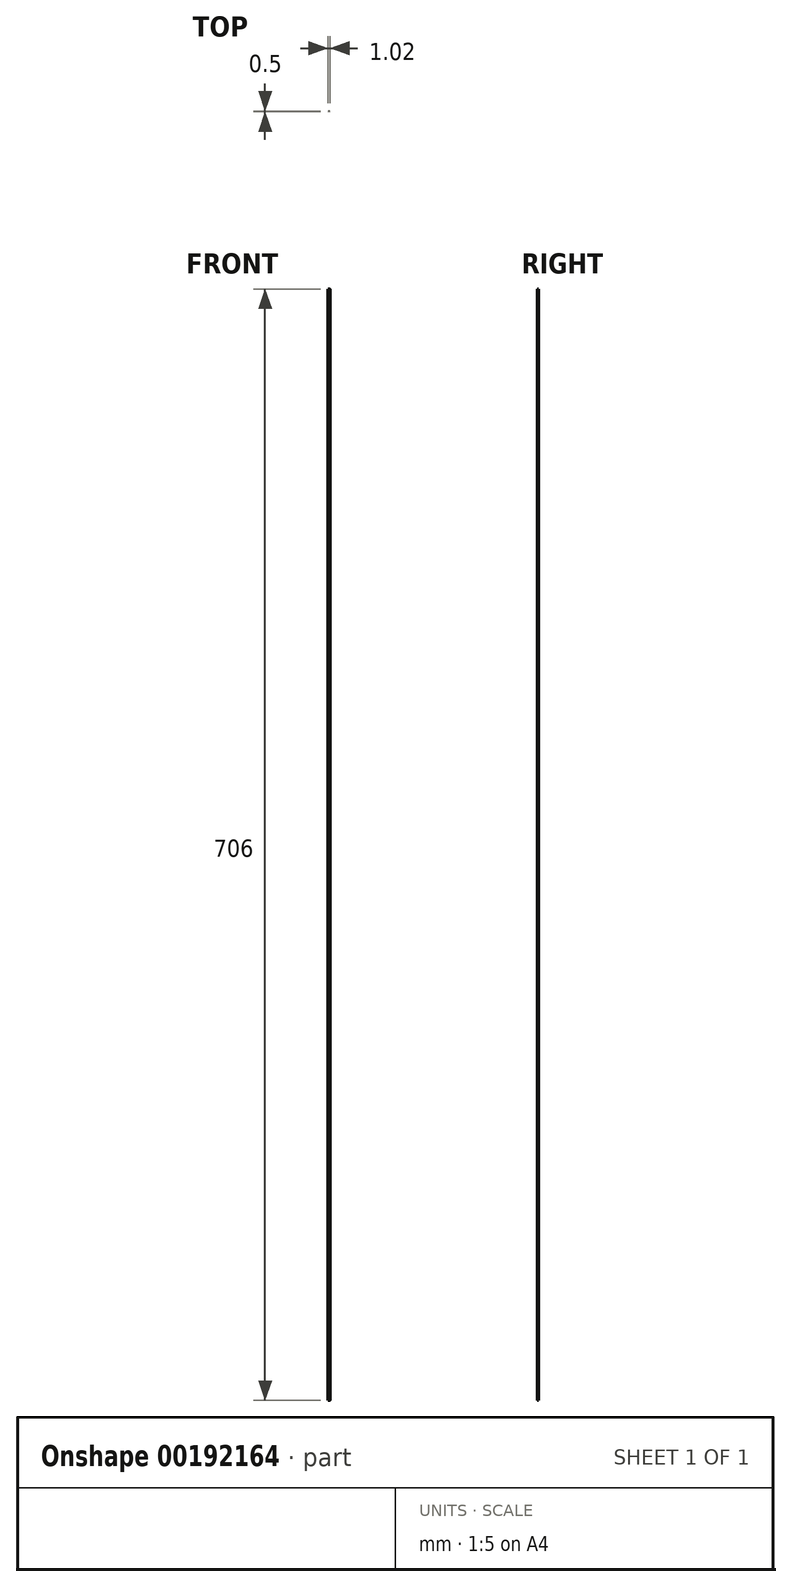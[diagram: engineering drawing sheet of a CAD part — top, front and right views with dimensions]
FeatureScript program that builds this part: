
annotation { "Feature Type Name" : "Feature", "Feature Type Description" : "" }
export const myFeature = defineFeature(function(context is Context, id is Id, definition is map)
    precondition{}
    {
        {
            var Q0;
            Q0=qCreatedBy(makeId("Top.planeOp"),FACE);
            var sketch = newSketch(context, id + "F0", { "sketchPlane" : qUnion([Q0])});
            skLineSegment(sketch, "E0.0", {"start": v(58.77, 41.7) * mm, "end": v(62.07, 38.4) * mm});
            skPoint(sketch, "E1.0", {"position": v(57.66, 41.92) * mm});
            skArc(sketch, "E2.0", {"start": v(57.02, 40.97) * mm, "mid": v(57.66, 41.92) * mm, "end": v(58.77, 41.7) * mm});
            skLineSegment(sketch, "E3.0", {"start": v(57.02, 38.85) * mm, "end": v(57.02, 40.97) * mm});
            skArc(sketch, "E4.0", {"start": v(55.97, 37.8) * mm, "mid": v(56.71, 38.11) * mm, "end": v(57.02, 38.85) * mm});
            skArc(sketch, "E5.0.0", {"start": v(63.56, 29.14) * mm, "mid": v(64.59, 29.83) * mm, "end": v(65.8, 30.07) * mm});
            skLineSegment(sketch, "E5.0.1", {"start": v(65.8, 30.07) * mm, "end": v(69.22, 30.07) * mm});
            skArc(sketch, "E5.0.2", {"start": v(69.22, 30.07) * mm, "mid": v(70.43, 29.83) * mm, "end": v(71.46, 29.14) * mm});
            skLineSegment(sketch, "E5.0.3", {"start": v(71.46, 29.14) * mm, "end": v(74.7, 25.92) * mm});
            skArc(sketch, "E5.0.4", {"start": v(74.7, 25.92) * mm, "mid": v(74.93, 24.74) * mm, "end": v(73.93, 24.08) * mm});
            skLineSegment(sketch, "E5.0.5", {"start": v(73.93, 24.08) * mm, "end": v(71.8, 24.08) * mm});
            skArc(sketch, "E5.0.6", {"start": v(71.8, 24.08) * mm, "mid": v(71.06, 23.77) * mm, "end": v(70.75, 23.03) * mm});
            skLineSegment(sketch, "E5.0.7", {"start": v(70.75, 23.03) * mm, "end": v(70.75, 22.92) * mm});
            skArc(sketch, "E5.0.8", {"start": v(70.75, 22.92) * mm, "mid": v(71.06, 22.17) * mm, "end": v(71.8, 21.87) * mm});
            skLineSegment(sketch, "E5.0.9", {"start": v(71.8, 21.87) * mm, "end": v(72.83, 21.87) * mm});
            skArc(sketch, "E5.0.10", {"start": v(72.83, 21.87) * mm, "mid": v(73.34, 22.37) * mm, "end": v(73.84, 21.87) * mm});
            skLineSegment(sketch, "E5.0.11", {"start": v(73.84, 21.87) * mm, "end": v(77.06, 21.87) * mm});
            skArc(sketch, "E5.0.12", {"start": v(77.06, 21.87) * mm, "mid": v(77.57, 22.37) * mm, "end": v(78.08, 21.87) * mm});
            skArc(sketch, "E5.0.13", {"start": v(78.08, 21.87) * mm, "mid": v(79.6, 22.48) * mm, "end": v(80.21, 24) * mm});
            skArc(sketch, "E5.0.14", {"start": v(80.21, 24) * mm, "mid": v(79.7, 24.5) * mm, "end": v(80.21, 25.02) * mm});
            skLineSegment(sketch, "E5.0.15", {"start": v(80.21, 25.02) * mm, "end": v(80.21, 28.23) * mm});
            skArc(sketch, "E5.0.16", {"start": v(80.21, 28.23) * mm, "mid": v(79.7, 28.74) * mm, "end": v(80.21, 29.25) * mm});
            skLineSegment(sketch, "E5.0.17", {"start": v(80.21, 29.25) * mm, "end": v(80.21, 30.28) * mm});
            skArc(sketch, "E5.0.18", {"start": v(80.21, 30.28) * mm, "mid": v(79.9, 31.02) * mm, "end": v(79.16, 31.33) * mm});
            skLineSegment(sketch, "E5.0.19", {"start": v(79.16, 31.33) * mm, "end": v(79.05, 31.33) * mm});
            skArc(sketch, "E5.0.20", {"start": v(79.05, 31.33) * mm, "mid": v(78.3, 31.02) * mm, "end": v(78, 30.28) * mm});
            skLineSegment(sketch, "E5.0.21", {"start": v(78, 30.28) * mm, "end": v(78, 28.16) * mm});
            skArc(sketch, "E5.0.22", {"start": v(78, 28.16) * mm, "mid": v(77.37, 27.21) * mm, "end": v(76.25, 27.44) * mm});
            skLineSegment(sketch, "E5.0.23", {"start": v(76.25, 27.44) * mm, "end": v(72.95, 30.73) * mm});
            skArc(sketch, "E5.0.24", {"start": v(72.95, 30.73) * mm, "mid": v(72.26, 31.76) * mm, "end": v(72.02, 32.97) * mm});
            skLineSegment(sketch, "E5.0.25", {"start": v(72.02, 32.97) * mm, "end": v(72.02, 36.16) * mm});
            skArc(sketch, "E5.0.26", {"start": v(72.02, 36.16) * mm, "mid": v(72.26, 37.38) * mm, "end": v(72.95, 38.4) * mm});
            skLineSegment(sketch, "E5.0.27", {"start": v(72.95, 38.4) * mm, "end": v(76.25, 41.7) * mm});
            skArc(sketch, "E5.0.28", {"start": v(76.25, 41.7) * mm, "mid": v(77.37, 41.92) * mm, "end": v(78, 40.97) * mm});
            skLineSegment(sketch, "E5.0.29", {"start": v(78, 40.97) * mm, "end": v(78, 38.85) * mm});
            skArc(sketch, "E5.0.30", {"start": v(78, 38.85) * mm, "mid": v(78.3, 38.11) * mm, "end": v(79.05, 37.8) * mm});
            skLineSegment(sketch, "E5.0.31", {"start": v(79.05, 37.8) * mm, "end": v(79.16, 37.8) * mm});
            skArc(sketch, "E5.0.32", {"start": v(79.16, 37.8) * mm, "mid": v(79.9, 38.11) * mm, "end": v(80.21, 38.85) * mm});
            skLineSegment(sketch, "E5.0.33", {"start": v(80.21, 38.85) * mm, "end": v(80.21, 39.88) * mm});
            skArc(sketch, "E5.0.34", {"start": v(80.21, 39.88) * mm, "mid": v(79.7, 40.4) * mm, "end": v(80.21, 40.9) * mm});
            skLineSegment(sketch, "E5.0.35", {"start": v(80.21, 40.9) * mm, "end": v(80.21, 44.12) * mm});
            skArc(sketch, "E5.0.36", {"start": v(80.21, 44.12) * mm, "mid": v(79.7, 44.62) * mm, "end": v(80.21, 45.13) * mm});
            skArc(sketch, "E5.0.37", {"start": v(80.21, 45.13) * mm, "mid": v(79.6, 46.65) * mm, "end": v(78.08, 47.27) * mm});
            skArc(sketch, "E5.0.38", {"start": v(78.08, 47.27) * mm, "mid": v(77.57, 46.76) * mm, "end": v(77.06, 47.27) * mm});
            skLineSegment(sketch, "E5.0.39", {"start": v(77.06, 47.27) * mm, "end": v(73.84, 47.27) * mm});
            skArc(sketch, "E5.0.40", {"start": v(73.84, 47.27) * mm, "mid": v(73.34, 46.76) * mm, "end": v(72.83, 47.27) * mm});
            skLineSegment(sketch, "E5.0.41", {"start": v(72.83, 47.27) * mm, "end": v(71.8, 47.27) * mm});
            skArc(sketch, "E5.0.42", {"start": v(71.8, 47.27) * mm, "mid": v(71.06, 46.96) * mm, "end": v(70.75, 46.22) * mm});
            skLineSegment(sketch, "E5.0.43", {"start": v(70.75, 46.22) * mm, "end": v(70.75, 46.1) * mm});
            skArc(sketch, "E5.0.44", {"start": v(70.75, 46.1) * mm, "mid": v(71.06, 45.36) * mm, "end": v(71.8, 45.06) * mm});
            skLineSegment(sketch, "E5.0.45", {"start": v(71.8, 45.06) * mm, "end": v(73.99, 45.06) * mm});
            skArc(sketch, "E5.0.46", {"start": v(73.99, 45.06) * mm, "mid": v(74.94, 44.42) * mm, "end": v(74.72, 43.3) * mm});
            skLineSegment(sketch, "E5.0.47", {"start": v(74.72, 43.3) * mm, "end": v(71.4, 39.99) * mm});
            skArc(sketch, "E5.0.48", {"start": v(71.4, 39.99) * mm, "mid": v(70.38, 39.3) * mm, "end": v(69.17, 39.06) * mm});
            skLineSegment(sketch, "E5.0.49", {"start": v(69.17, 39.06) * mm, "end": v(65.86, 39.06) * mm});
            skArc(sketch, "E5.0.50", {"start": v(65.86, 39.06) * mm, "mid": v(64.64, 39.3) * mm, "end": v(63.61, 39.99) * mm});
            skLineSegment(sketch, "E5.0.51", {"start": v(63.61, 39.99) * mm, "end": v(60.3, 43.3) * mm});
            skArc(sketch, "E5.0.52", {"start": v(60.3, 43.3) * mm, "mid": v(60.08, 44.42) * mm, "end": v(61.03, 45.06) * mm});
            skLineSegment(sketch, "E5.0.53", {"start": v(61.03, 45.06) * mm, "end": v(63.22, 45.06) * mm});
            skArc(sketch, "E5.0.54", {"start": v(63.22, 45.06) * mm, "mid": v(63.97, 45.36) * mm, "end": v(64.27, 46.1) * mm});
            skLineSegment(sketch, "E5.0.55", {"start": v(64.27, 46.1) * mm, "end": v(64.27, 46.22) * mm});
            skArc(sketch, "E5.0.56", {"start": v(64.27, 46.22) * mm, "mid": v(63.97, 46.96) * mm, "end": v(63.22, 47.27) * mm});
            skLineSegment(sketch, "E5.0.57", {"start": v(63.22, 47.27) * mm, "end": v(62.2, 47.27) * mm});
            skArc(sketch, "E5.0.58", {"start": v(62.2, 47.27) * mm, "mid": v(61.69, 46.76) * mm, "end": v(61.18, 47.27) * mm});
            skLineSegment(sketch, "E5.0.59", {"start": v(61.18, 47.27) * mm, "end": v(57.96, 47.27) * mm});
            skArc(sketch, "E5.0.60", {"start": v(57.96, 47.27) * mm, "mid": v(57.45, 46.76) * mm, "end": v(56.95, 47.27) * mm});
            skArc(sketch, "E5.0.61", {"start": v(56.95, 47.27) * mm, "mid": v(55.43, 46.65) * mm, "end": v(54.81, 45.13) * mm});
            skArc(sketch, "E5.0.62", {"start": v(54.81, 45.13) * mm, "mid": v(55.32, 44.62) * mm, "end": v(54.81, 44.12) * mm});
            skLineSegment(sketch, "E5.0.63", {"start": v(54.81, 44.12) * mm, "end": v(54.81, 40.9) * mm});
            skArc(sketch, "E5.0.64", {"start": v(54.81, 40.9) * mm, "mid": v(55.32, 40.4) * mm, "end": v(54.81, 39.88) * mm});
            skLineSegment(sketch, "E5.0.65", {"start": v(54.81, 39.88) * mm, "end": v(54.81, 38.85) * mm});
            skArc(sketch, "E5.0.66", {"start": v(54.81, 38.85) * mm, "mid": v(55.12, 38.11) * mm, "end": v(55.86, 37.8) * mm});
            skLineSegment(sketch, "E5.0.67", {"start": v(55.86, 37.8) * mm, "end": v(55.97, 37.8) * mm});
            skArc(sketch, "E5.0.72", {"start": v(62.07, 38.4) * mm, "mid": v(62.76, 37.38) * mm, "end": v(63, 36.16) * mm});
            skLineSegment(sketch, "E5.0.73", {"start": v(63, 36.16) * mm, "end": v(63, 32.97) * mm});
            skArc(sketch, "E5.0.74", {"start": v(63, 32.97) * mm, "mid": v(62.76, 31.76) * mm, "end": v(62.07, 30.73) * mm});
            skLineSegment(sketch, "E5.0.75", {"start": v(62.07, 30.73) * mm, "end": v(58.77, 27.44) * mm});
            skArc(sketch, "E5.0.76", {"start": v(58.77, 27.44) * mm, "mid": v(57.66, 27.21) * mm, "end": v(57.02, 28.16) * mm});
            skLineSegment(sketch, "E5.0.77", {"start": v(57.02, 28.16) * mm, "end": v(57.02, 30.28) * mm});
            skArc(sketch, "E5.0.78", {"start": v(57.02, 30.28) * mm, "mid": v(56.71, 31.02) * mm, "end": v(55.97, 31.33) * mm});
            skLineSegment(sketch, "E5.0.79", {"start": v(55.97, 31.33) * mm, "end": v(55.86, 31.33) * mm});
            skArc(sketch, "E5.0.80", {"start": v(55.86, 31.33) * mm, "mid": v(55.12, 31.02) * mm, "end": v(54.81, 30.28) * mm});
            skLineSegment(sketch, "E5.0.81", {"start": v(54.81, 30.28) * mm, "end": v(54.81, 29.25) * mm});
            skArc(sketch, "E5.0.82", {"start": v(54.81, 29.25) * mm, "mid": v(55.32, 28.74) * mm, "end": v(54.81, 28.23) * mm});
            skLineSegment(sketch, "E5.0.83", {"start": v(54.81, 28.23) * mm, "end": v(54.81, 25.02) * mm});
            skArc(sketch, "E5.0.84", {"start": v(54.81, 25.02) * mm, "mid": v(55.32, 24.5) * mm, "end": v(54.81, 24) * mm});
            skArc(sketch, "E5.0.85", {"start": v(54.81, 24) * mm, "mid": v(55.43, 22.48) * mm, "end": v(56.95, 21.87) * mm});
            skArc(sketch, "E5.0.86", {"start": v(56.95, 21.87) * mm, "mid": v(57.45, 22.37) * mm, "end": v(57.96, 21.87) * mm});
            skLineSegment(sketch, "E5.0.87", {"start": v(57.96, 21.87) * mm, "end": v(61.18, 21.87) * mm});
            skArc(sketch, "E5.0.88", {"start": v(61.18, 21.87) * mm, "mid": v(61.69, 22.37) * mm, "end": v(62.2, 21.87) * mm});
            skLineSegment(sketch, "E5.0.89", {"start": v(62.2, 21.87) * mm, "end": v(63.22, 21.87) * mm});
            skArc(sketch, "E5.0.90", {"start": v(63.22, 21.87) * mm, "mid": v(63.97, 22.17) * mm, "end": v(64.27, 22.92) * mm});
            skLineSegment(sketch, "E5.0.91", {"start": v(64.27, 22.92) * mm, "end": v(64.27, 23.03) * mm});
            skArc(sketch, "E5.0.92", {"start": v(64.27, 23.03) * mm, "mid": v(63.97, 23.77) * mm, "end": v(63.22, 24.08) * mm});
            skLineSegment(sketch, "E5.0.93", {"start": v(63.22, 24.08) * mm, "end": v(61.1, 24.08) * mm});
            skArc(sketch, "E5.0.94", {"start": v(61.1, 24.08) * mm, "mid": v(60.1, 24.74) * mm, "end": v(60.33, 25.92) * mm});
            skLineSegment(sketch, "E5.0.95", {"start": v(60.33, 25.92) * mm, "end": v(63.56, 29.14) * mm});
            skSolve(sketch);
        }
        {
            var Q0;
            Q0=makeQuery(id+"F0.imprint","IMPRINT",FACE,{"disambiguationData":[TD([[makeQuery(id+"F0.imprint","IMPRINT",EDGE,{"derivedFrom":sQuery(id+"F0.wireOp",EDGE,"E5.0.12")}),1.0]])]});
            extrude(context, id + "F1", {"entities" : qUnion([Q0]), "depth" : 706 * mm});
        }
    });
